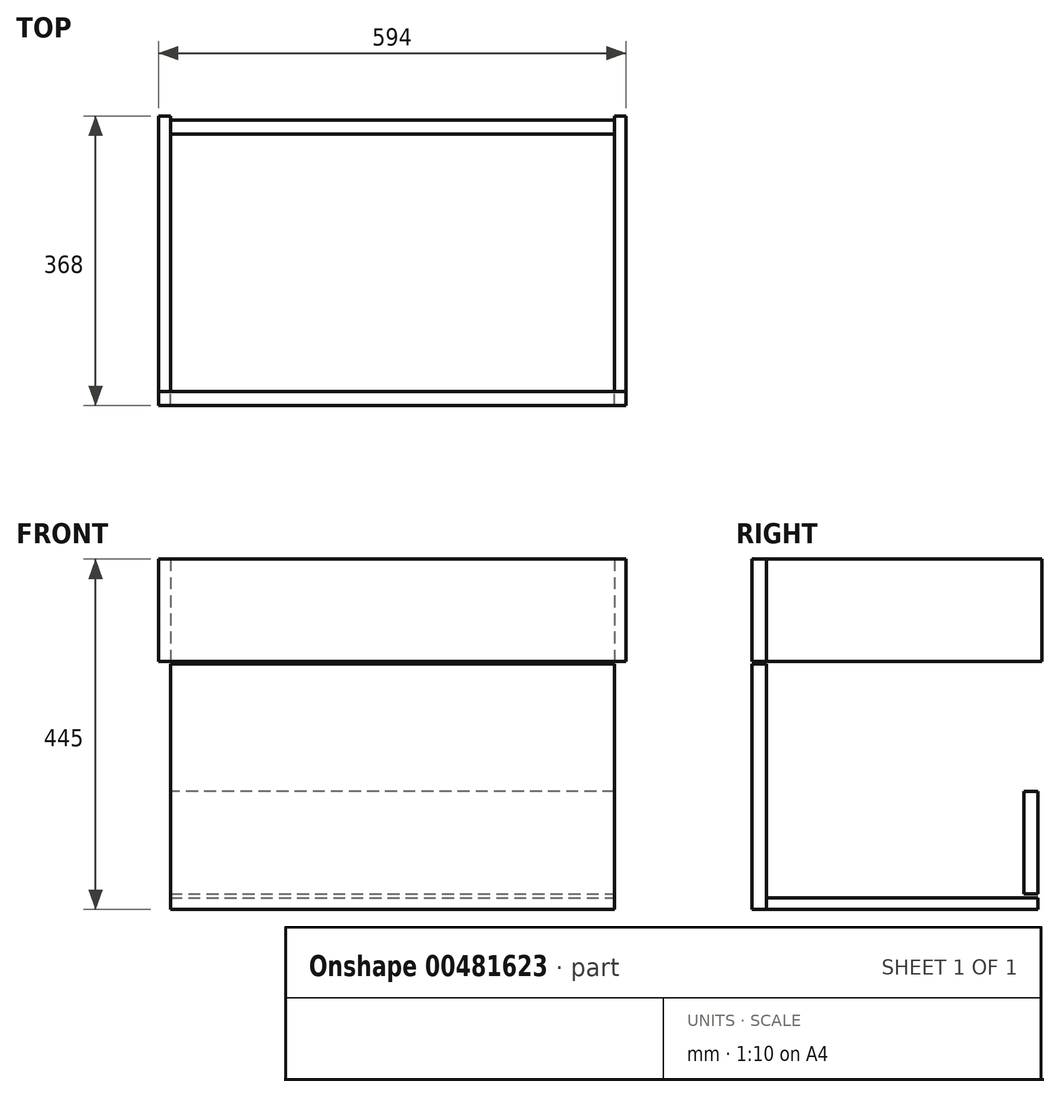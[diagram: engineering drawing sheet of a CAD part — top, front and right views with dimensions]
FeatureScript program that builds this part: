
annotation { "Feature Type Name" : "Feature", "Feature Type Description" : "" }
export const myFeature = defineFeature(function(context is Context, id is Id, definition is map)
    precondition{}
    {
        {
            var Q0;
            Q0=qCreatedBy(makeId("Front.planeOp"),FACE);
            var sketch = newSketch(context, id + "F0", { "sketchPlane" : qUnion([Q0])});
            skLineSegment(sketch, "E0.bottom", {"start": v(300, 225.5) * mm, "end": v(-300, 225.5) * mm});
            skLineSegment(sketch, "E0.top", {"start": v(300, -225.5) * mm, "end": v(-300, -225.5) * mm});
            skLineSegment(sketch, "E0.left", {"start": v(300, 225.5) * mm, "end": v(300, -225.5) * mm});
            skLineSegment(sketch, "E0.right", {"start": v(-300, 225.5) * mm, "end": v(-300, -225.5) * mm});
            skPoint(sketch, "E0.middle", {"position": v(0, 0) * mm});
            skLineSegment(sketch, "E1.bottom", {"start": v(-300, 225.5) * mm, "end": v(-282, 225.5) * mm});
            skLineSegment(sketch, "E1.top", {"start": v(-300, -225.5) * mm, "end": v(-282, -225.5) * mm});
            skLineSegment(sketch, "E1.right", {"start": v(-282, 225.5) * mm, "end": v(-282, -225.5) * mm});
            skLineSegment(sketch, "E2", {"start": v(0, 225.5) * mm, "end": v(0, -225.5) * mm, "construction": true});
            skLineSegment(sketch, "E3.MirrorCS", {"start": v(282, 225.5) * mm, "end": v(282, -225.5) * mm});
            skLineSegment(sketch, "E4.MirrorCS", {"start": v(300, 225.5) * mm, "end": v(282, 225.5) * mm});
            skLineSegment(sketch, "E5.MirrorCS", {"start": v(300, -225.5) * mm, "end": v(282, -225.5) * mm});
            skLineSegment(sketch, "E6.bottom", {"start": v(-282, -225.5) * mm, "end": v(282, -225.5) * mm});
            skLineSegment(sketch, "E6.top", {"start": v(-282, -207.5) * mm, "end": v(282, -207.5) * mm});
            skLineSegment(sketch, "E6.left", {"start": v(-282, -225.5) * mm, "end": v(-282, -207.5) * mm});
            skLineSegment(sketch, "E6.right", {"start": v(282, -225.5) * mm, "end": v(282, -207.5) * mm});
            skLineSegment(sketch, "E7.bottom", {"start": v(-282, -202.5) * mm, "end": v(282, -202.5) * mm});
            skLineSegment(sketch, "E7.top", {"start": v(-282, -72.5) * mm, "end": v(282, -72.5) * mm});
            skLineSegment(sketch, "E7.left", {"start": v(-282, -202.5) * mm, "end": v(-282, -72.5) * mm});
            skLineSegment(sketch, "E7.right", {"start": v(282, -202.5) * mm, "end": v(282, -72.5) * mm});
            skPoint(sketch, "E8.firstSnap0", {"position": v(-291, 225.5) * mm});
            skLineSegment(sketch, "E9.bottom", {"start": v(-297, 92.5) * mm, "end": v(297, 92.5) * mm});
            skLineSegment(sketch, "E9.top", {"start": v(-297, 222.5) * mm, "end": v(297, 222.5) * mm});
            skLineSegment(sketch, "E9.left", {"start": v(-297, 92.5) * mm, "end": v(-297, 222.5) * mm});
            skLineSegment(sketch, "E9.right", {"start": v(297, 92.5) * mm, "end": v(297, 222.5) * mm});
            skLineSegment(sketch, "E10.bottom", {"start": v(-297, 89.5) * mm, "end": v(297, 89.5) * mm});
            skLineSegment(sketch, "E10.top", {"start": v(-297, -222.5) * mm, "end": v(297, -222.5) * mm});
            skLineSegment(sketch, "E10.left", {"start": v(-297, 89.5) * mm, "end": v(-297, -222.5) * mm});
            skLineSegment(sketch, "E10.right", {"start": v(297, 89.5) * mm, "end": v(297, -222.5) * mm});
            skSolve(sketch);
        }
        {
            var Q0;
            {var subQ5=sQuery(id+"F0.wireOp",EDGE,"E9.left");Q0=makeQuery(id+"F0.imprint","IMPRINT",FACE,{"disambiguationData":[TD([[makeQuery(id+"F0.imprint","IMPRINT",EDGE,{"derivedFrom":subQ5}),-1.0]])]});}
            var Q1;
            {var subQ0=sQuery(id+"F0.wireOp",EDGE,"E7.left");Q1=makeQuery(id+"F0.imprint","IMPRINT",FACE,{"disambiguationData":[TD([[makeQuery(id+"F0.imprint","IMPRINT",EDGE,{"derivedFrom":subQ0}),1.0]])]});}
            var Q2;
            {var subQ4=sQuery(id+"F0.wireOp",EDGE,"E1.bottom");Q2=makeQuery(id+"F0.imprint","IMPRINT",FACE,{"disambiguationData":[TD([[makeQuery(id+"F0.imprint","IMPRINT",EDGE,{"derivedFrom":subQ4}),-1.0]])]});}
            var Q3;
            {var subQ8=sQuery(id+"F0.wireOp",EDGE,"E4.MirrorCS");Q3=makeQuery(id+"F0.imprint","IMPRINT",FACE,{"disambiguationData":[TD([[makeQuery(id+"F0.imprint","IMPRINT",EDGE,{"derivedFrom":subQ8}),1.0]])]});}
            var Q4;
            {var subQ5=sQuery(id+"F0.wireOp",EDGE,"E9.right");Q4=makeQuery(id+"F0.imprint","IMPRINT",FACE,{"disambiguationData":[TD([[makeQuery(id+"F0.imprint","IMPRINT",EDGE,{"derivedFrom":subQ5}),1.0]])]});}
            var Q5;
            {var subQ0=sQuery(id+"F0.wireOp",EDGE,"E7.right");Q5=makeQuery(id+"F0.imprint","IMPRINT",FACE,{"disambiguationData":[TD([[makeQuery(id+"F0.imprint","IMPRINT",EDGE,{"derivedFrom":subQ0}),-1.0]])]});}
            extrude(context, id + "F1", {"entities" : qUnion([Q0, Q1, Q2, Q3, Q4, Q5]), "oppositeDirection" : true, "depth" : 350 * mm});
        }
        {
            var Q0;
            {var subQ0=sQuery(id+"F0.wireOp",EDGE,"E6.bottom");Q0=makeQuery(id+"F0.imprint","IMPRINT",FACE,{"disambiguationData":[TD([[makeQuery(id+"F0.imprint","IMPRINT",EDGE,{"derivedFrom":subQ0}),1.0]])]});}
            var Q1;
            {var subQ0=sQuery(id+"F0.wireOp",EDGE,"E6.top");Q1=makeQuery(id+"F0.imprint","IMPRINT",FACE,{"disambiguationData":[TD([[makeQuery(id+"F0.imprint","IMPRINT",EDGE,{"derivedFrom":subQ0}),-1.0]])]});}
            extrude(context, id + "F2", {"entities" : qUnion([Q0, Q1]), "oppositeDirection" : true, "depth" : 345 * mm});
        }
        {
            var Q0;
            Q0=makeQuery(id+"F2.opExtrude","CAP_FACE",FACE,{"disambiguationData":[OSD([sQuery(id+"F0.wireOp",EDGE,"E6.bottom"),sQuery(id+"F0.wireOp",EDGE,"E6.top"),sQuery(id+"F0.wireOp",EDGE,"E6.left"),sQuery(id+"F0.wireOp",EDGE,"E6.right")])],"isStart":false});
            var sketch = newSketch(context, id + "F3", { "sketchPlane" : qUnion([Q0])});
            skLineSegment(sketch, "E11.0.0", {"start": v(282, -72.5) * mm, "end": v(282, -202.5) * mm});
            skLineSegment(sketch, "E11.0.1", {"start": v(282, -202.5) * mm, "end": v(-282, -202.5) * mm});
            skLineSegment(sketch, "E11.0.2", {"start": v(-282, -202.5) * mm, "end": v(-282, -72.5) * mm});
            skLineSegment(sketch, "E11.0.3", {"start": v(-282, -72.5) * mm, "end": v(282, -72.5) * mm});
            skSolve(sketch);
        }
        {
            var Q0;
            Q0 = qSketchRegion(id + "F3", true);
            extrude(context, id + "F4", {"entities" : qUnion([Q0]), "oppositeDirection" : true, "depth" : 18 * mm});
        }
        {
            var Q0;
            {var subQ0=sQuery(id+"F0.wireOp",EDGE,"E7.left");Q0=makeQuery(id+"F0.imprint","IMPRINT",FACE,{"disambiguationData":[TD([[makeQuery(id+"F0.imprint","IMPRINT",EDGE,{"derivedFrom":subQ0}),1.0]])]});}
            var Q1;
            {var subQ0=sQuery(id+"F0.wireOp",EDGE,"E7.top");Q1=makeQuery(id+"F0.imprint","IMPRINT",FACE,{"disambiguationData":[TD([[makeQuery(id+"F0.imprint","IMPRINT",EDGE,{"derivedFrom":subQ0}),1.0]])]});}
            var Q2;
            {var subQ0=sQuery(id+"F0.wireOp",EDGE,"E7.right");Q2=makeQuery(id+"F0.imprint","IMPRINT",FACE,{"disambiguationData":[TD([[makeQuery(id+"F0.imprint","IMPRINT",EDGE,{"derivedFrom":subQ0}),-1.0]])]});}
            var Q3;
            Q3=makeQuery(id+"F0.imprint","IMPRINT",FACE,{"disambiguationData":[TD([[makeQuery(id+"F0.imprint","IMPRINT",EDGE,{"derivedFrom":sQuery(id+"F0.wireOp",EDGE,"E7.bottom")}),1.0]])]});
            var Q4;
            {var subQ0=sQuery(id+"F0.wireOp",EDGE,"E6.top");Q4=makeQuery(id+"F0.imprint","IMPRINT",FACE,{"disambiguationData":[TD([[makeQuery(id+"F0.imprint","IMPRINT",EDGE,{"derivedFrom":subQ0}),1.0]])]});}
            var Q5;
            {var subQ0=sQuery(id+"F0.wireOp",EDGE,"E6.top");Q5=makeQuery(id+"F0.imprint","IMPRINT",FACE,{"disambiguationData":[TD([[makeQuery(id+"F0.imprint","IMPRINT",EDGE,{"derivedFrom":subQ0}),-1.0]])]});}
            var Q6;
            {var subQ0=sQuery(id+"F0.wireOp",EDGE,"E9.top");var subQ1=sQuery(id+"F0.wireOp",EDGE,"E1.right");var subQ2=makeQuery(id+"F0.imprint","INTERSECT",VERTEX,{"derivedFrom":[subQ1,subQ0]});Q6=makeQuery(id+"F0.imprint","IMPRINT",FACE,{"disambiguationData":[TD([[makeQuery(id+"F0.imprint","IMPRINT",EDGE,{"disambiguationData":[TD([[subQ2,-1.0]])],"derivedFrom":subQ1}),1.0]])]});}
            var Q7;
            {var subQ5=sQuery(id+"F0.wireOp",EDGE,"E9.left");Q7=makeQuery(id+"F0.imprint","IMPRINT",FACE,{"disambiguationData":[TD([[makeQuery(id+"F0.imprint","IMPRINT",EDGE,{"derivedFrom":subQ5}),-1.0]])]});}
            var Q8;
            {var subQ5=sQuery(id+"F0.wireOp",EDGE,"E9.right");Q8=makeQuery(id+"F0.imprint","IMPRINT",FACE,{"disambiguationData":[TD([[makeQuery(id+"F0.imprint","IMPRINT",EDGE,{"derivedFrom":subQ5}),1.0]])]});}
            extrude(context, id + "F5", {"entities" : qUnion([Q0, Q1, Q2, Q3, Q4, Q5, Q6, Q7, Q8]), "depth" : 18 * mm});
        }
    });
